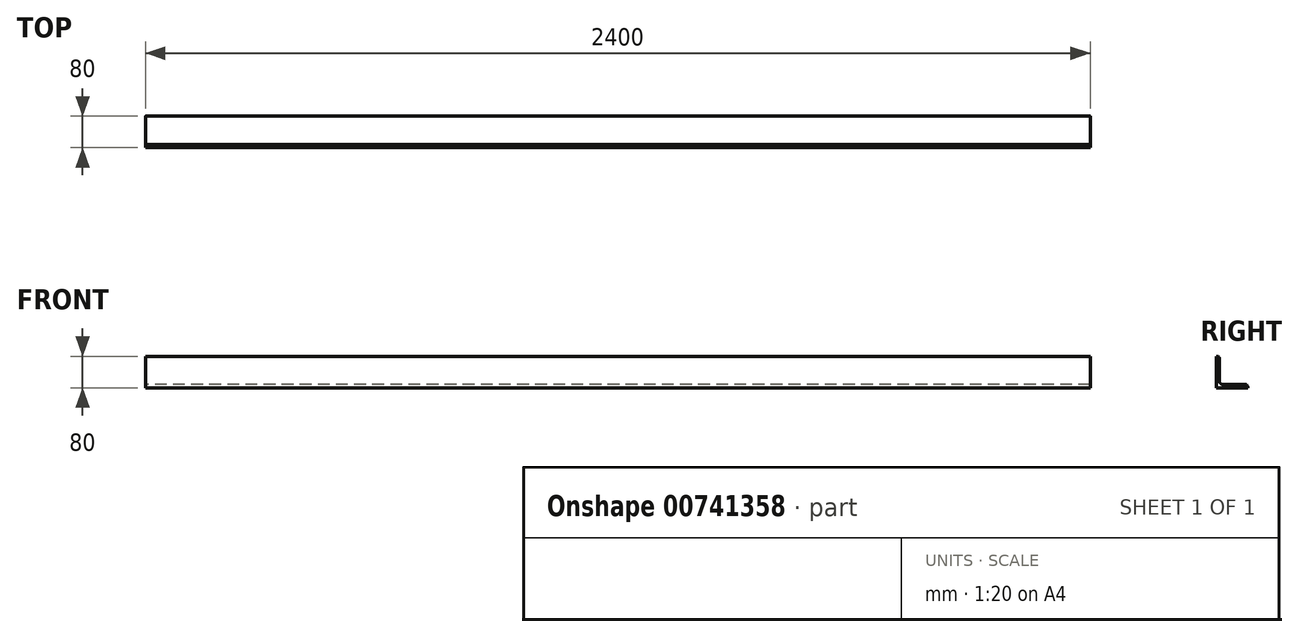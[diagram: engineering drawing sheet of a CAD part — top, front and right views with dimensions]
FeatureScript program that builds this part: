
annotation { "Feature Type Name" : "Feature", "Feature Type Description" : "" }
export const myFeature = defineFeature(function(context is Context, id is Id, definition is map)
    precondition{}
    {
        {
            var Q0;
            Q0=qCreatedBy(makeId("Right.planeOp"),FACE);
            var sketch = newSketch(context, id + "F0", { "sketchPlane" : qUnion([Q0])});
            skLineSegment(sketch, "E0", {"start": v(136.93, -53.3) * mm, "end": v(56.93, -53.3) * mm});
            skLineSegment(sketch, "E1", {"start": v(56.93, -53.3) * mm, "end": v(56.93, 26.7) * mm});
            skLineSegment(sketch, "E2", {"start": v(136.93, -53.3) * mm, "end": v(136.93, -50.3) * mm});
            skLineSegment(sketch, "E3", {"start": v(131.93, -45.3) * mm, "end": v(74.93, -45.3) * mm});
            skLineSegment(sketch, "E4", {"start": v(64.93, -35.3) * mm, "end": v(64.93, 21.7) * mm});
            skLineSegment(sketch, "E5", {"start": v(59.93, 26.7) * mm, "end": v(56.93, 26.7) * mm});
            skPoint(sketch, "E6.visualSharp", {"position": v(64.93, 26.7) * mm});
            skArc(sketch, "E6.filletArc", {"start": v(64.93, 21.7) * mm, "mid": v(63.47, 25.23) * mm, "end": v(59.93, 26.7) * mm});
            skPoint(sketch, "E7.visualSharp", {"position": v(136.93, -45.3) * mm});
            skArc(sketch, "E7.filletArc", {"start": v(136.93, -50.3) * mm, "mid": v(135.47, -46.77) * mm, "end": v(131.93, -45.3) * mm});
            skPoint(sketch, "E8.visualSharp", {"position": v(64.93, -45.3) * mm});
            skArc(sketch, "E8.filletArc", {"start": v(64.93, -35.3) * mm, "mid": v(67.86, -42.37) * mm, "end": v(74.93, -45.3) * mm});
            skSolve(sketch);
        }
        {
            var Q0;
            Q0=makeQuery(id+"F0.imprint","IMPRINT",FACE,{"disambiguationData":[TD([[makeQuery(id+"F0.imprint","IMPRINT",EDGE,{"derivedFrom":sQuery(id+"F0.wireOp",EDGE,"E0")}),-1.0]])]});
            extrude(context, id + "F1", {"entities" : qUnion([Q0]), "endBound" : BoundingType.SYMMETRIC, "depth" : 2400 * mm, "offsetDistance" : 25 * mm});
        }
    });
